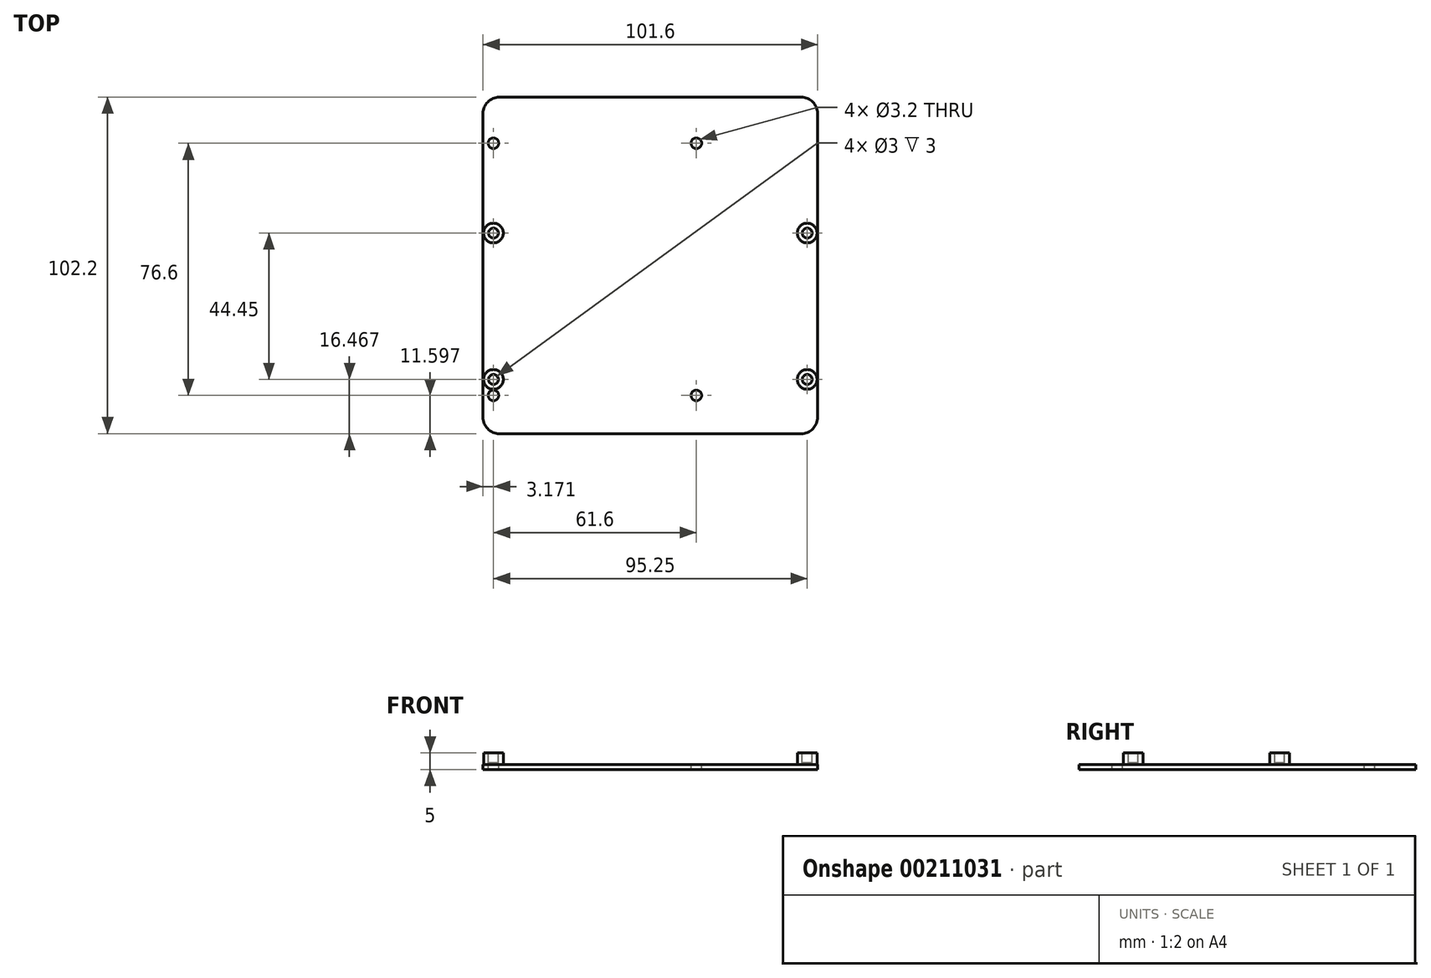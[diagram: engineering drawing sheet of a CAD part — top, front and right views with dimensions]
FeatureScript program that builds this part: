
annotation { "Feature Type Name" : "Feature", "Feature Type Description" : "" }
export const myFeature = defineFeature(function(context is Context, id is Id, definition is map)
    precondition{}
    {
        {
            var Q0;
            Q0=qCreatedBy(makeId("Top.planeOp"),FACE);
            var sketch = newSketch(context, id + "F0", { "sketchPlane" : qUnion([Q0])});
            skLineSegment(sketch, "E0.bottom", {"start": v(-70.53, 110.53) * mm, "end": v(31.07, 110.53) * mm});
            skLineSegment(sketch, "E0.top", {"start": v(-70.53, -36.47) * mm, "end": v(31.07, -36.47) * mm});
            skLineSegment(sketch, "E0.left", {"start": v(-70.53, 110.53) * mm, "end": v(-70.53, -36.47) * mm});
            skLineSegment(sketch, "E0.right", {"start": v(31.07, 110.53) * mm, "end": v(31.07, -36.47) * mm});
            skCircle(sketch, "E1", {"center": v(-67.36, 69.25) * mm, "radius": 3 * mm});
            skCircle(sketch, "E2", {"center": v(27.9, 69.25) * mm, "radius": 3 * mm});
            skCircle(sketch, "E3", {"center": v(-67.36, 24.8) * mm, "radius": 3 * mm});
            skCircle(sketch, "E4", {"center": v(27.9, 24.8) * mm, "radius": 3 * mm});
            skSolve(sketch);
        }
        {
            var Q0;
            Q0=makeQuery(id+"F0.imprint","IMPRINT",FACE,{"disambiguationData":[TD([[makeQuery(id+"F0.imprint","IMPRINT",EDGE,{"derivedFrom":sQuery(id+"F0.wireOp",EDGE,"E1")}),-1.0]])]});
            var Q1;
            {var subQ8=sQuery(id+"F0.wireOp",EDGE,"E0.bottom");Q1=makeQuery(id+"F0.imprint","IMPRINT",FACE,{"disambiguationData":[TD([[makeQuery(id+"F0.imprint","IMPRINT",EDGE,{"derivedFrom":subQ8}),-1.0]])]});}
            var Q2;
            Q2=makeQuery(id+"F0.imprint","IMPRINT",FACE,{"disambiguationData":[TD([[makeQuery(id+"F0.imprint","IMPRINT",EDGE,{"derivedFrom":sQuery(id+"F0.wireOp",EDGE,"E3")}),-1.0]])]});
            var Q3;
            Q3=makeQuery(id+"F0.imprint","IMPRINT",FACE,{"disambiguationData":[TD([[makeQuery(id+"F0.imprint","IMPRINT",EDGE,{"derivedFrom":sQuery(id+"F0.wireOp",EDGE,"E2")}),-1.0]])]});
            var Q4;
            Q4=makeQuery(id+"F0.imprint","IMPRINT",FACE,{"disambiguationData":[TD([[makeQuery(id+"F0.imprint","IMPRINT",EDGE,{"derivedFrom":sQuery(id+"F0.wireOp",EDGE,"E4")}),-1.0]])]});
            var Q5;
            {var subQ0=sQuery(id+"F0.wireOp",EDGE,"LZDnmpIZ-xvqJ-npT3-o2hn-prvxRaRxMuR7");var subQ1=sQuery(id+"F0.wireOp",EDGE,"E0.right");var subQ2=makeQuery(id+"F0.imprint","INTERSECT",VERTEX,{"disambiguationData":[OD(0.0)],"derivedFrom":[subQ1,subQ0]});Q5=makeQuery(id+"F0.imprint","IMPRINT",FACE,{"disambiguationData":[TD([[makeQuery(id+"F0.imprint","IMPRINT",EDGE,{"disambiguationData":[TD([[subQ2,-1.0]])],"derivedFrom":subQ1}),1.0]])]});}
            var Q6;
            {var subQ0=sQuery(id+"F0.wireOp",EDGE,"yrvKWCMc-wCms-miBF-EHxo-dlBtZxVLjjzE");var subQ1=sQuery(id+"F0.wireOp",EDGE,"E0.right");var subQ2=makeQuery(id+"F0.imprint","INTERSECT",VERTEX,{"disambiguationData":[OD(0.0)],"derivedFrom":[subQ1,subQ0]});Q6=makeQuery(id+"F0.imprint","IMPRINT",FACE,{"disambiguationData":[TD([[makeQuery(id+"F0.imprint","IMPRINT",EDGE,{"disambiguationData":[TD([[subQ2,-1.0]])],"derivedFrom":subQ1}),1.0]])]});}
            extrude(context, id + "F1", {"entities" : qUnion([Q0, Q1, Q2, Q3, Q4, Q5, Q6]), "depth" : 1.5 * mm});
        }
        {
            var Q0;
            Q0=makeQuery(id+"F1.opExtrude","CAP_FACE",FACE,{"disambiguationData":[OSD([sQuery(id+"F0.wireOp",EDGE,"E0.bottom"),sQuery(id+"F0.wireOp",EDGE,"E0.top"),sQuery(id+"F0.wireOp",EDGE,"E0.left"),sQuery(id+"F0.wireOp",EDGE,"E0.right"),sQuery(id+"F0.wireOp",EDGE,"E1"),sQuery(id+"F0.wireOp",EDGE,"E2"),sQuery(id+"F0.wireOp",EDGE,"E3"),sQuery(id+"F0.wireOp",EDGE,"E4"),sQuery(id+"F0.wireOp",EDGE,"YPoFhnEZ-2VS0-5aPg-Brrl-id8hAxNxdBGg"),sQuery(id+"F0.wireOp",EDGE,"uQWfn0jv-DCcC-0w1e-9Akf-fMqCXPyrSpFM"),sQuery(id+"F0.wireOp",EDGE,"LZDnmpIZ-xvqJ-npT3-o2hn-prvxRaRxMuR7"),sQuery(id+"F0.wireOp",EDGE,"yrvKWCMc-wCms-miBF-EHxo-dlBtZxVLjjzE")])],"isStart":false});
            var sketch = newSketch(context, id + "F2", { "sketchPlane" : qUnion([Q0])});
            skPoint(sketch, "E5.0", {"position": v(-67.36, 69.25) * mm});
            skCircle(sketch, "E6", {"center": v(-67.36, 96.53) * mm, "radius": 1.6 * mm});
            skCircle(sketch, "E7", {"center": v(-67.36, 19.93) * mm, "radius": 1.6 * mm});
            skCircle(sketch, "E8", {"center": v(-5.76, 96.53) * mm, "radius": 1.6 * mm});
            skCircle(sketch, "E9", {"center": v(-5.76, 19.93) * mm, "radius": 1.6 * mm});
            skSolve(sketch);
        }
        {
            var Q0;
            Q0=makeQuery(id+"F2.imprint","IMPRINT",FACE,{"disambiguationData":[TD([[makeQuery(id+"F2.imprint","IMPRINT",EDGE,{"derivedFrom":sQuery(id+"F2.wireOp",EDGE,"E6")}),1.0]])]});
            var Q1;
            Q1=makeQuery(id+"F2.imprint","IMPRINT",FACE,{"disambiguationData":[TD([[makeQuery(id+"F2.imprint","IMPRINT",EDGE,{"derivedFrom":sQuery(id+"F2.wireOp",EDGE,"E8")}),1.0]])]});
            var Q2;
            Q2=makeQuery(id+"F2.imprint","IMPRINT",FACE,{"disambiguationData":[TD([[makeQuery(id+"F2.imprint","IMPRINT",EDGE,{"derivedFrom":sQuery(id+"F2.wireOp",EDGE,"E7")}),1.0]])]});
            var Q3;
            Q3=makeQuery(id+"F2.imprint","IMPRINT",FACE,{"disambiguationData":[TD([[makeQuery(id+"F2.imprint","IMPRINT",EDGE,{"derivedFrom":sQuery(id+"F2.wireOp",EDGE,"E9")}),1.0]])]});
            extrude(context, id + "F3", {"entities" : qUnion([Q0, Q1, Q2, Q3]), "operationType" : NewBodyOperationType.REMOVE, "oppositeDirection" : true, "depth" : 25 * mm});
        }
        {
            var Q0;
            Q0=makeQuery(id+"F0.imprint","IMPRINT",FACE,{"disambiguationData":[TD([[makeQuery(id+"F0.imprint","IMPRINT",EDGE,{"derivedFrom":sQuery(id+"F0.wireOp",EDGE,"E1")}),1.0]])]});
            var Q1;
            Q1=makeQuery(id+"F0.imprint","IMPRINT",FACE,{"disambiguationData":[TD([[makeQuery(id+"F0.imprint","IMPRINT",EDGE,{"derivedFrom":sQuery(id+"F0.wireOp",EDGE,"E3")}),1.0]])]});
            var Q2;
            Q2=makeQuery(id+"F0.imprint","IMPRINT",FACE,{"disambiguationData":[TD([[makeQuery(id+"F0.imprint","IMPRINT",EDGE,{"derivedFrom":sQuery(id+"F0.wireOp",EDGE,"E2")}),1.0]])]});
            var Q3;
            Q3=makeQuery(id+"F0.imprint","IMPRINT",FACE,{"disambiguationData":[TD([[makeQuery(id+"F0.imprint","IMPRINT",EDGE,{"derivedFrom":sQuery(id+"F0.wireOp",EDGE,"E4")}),1.0]])]});
            extrude(context, id + "F4", {"entities" : qUnion([Q0, Q1, Q2, Q3]), "operationType" : NewBodyOperationType.ADD, "depth" : 5 * mm});
        }
        {
            var Q0;
            Q0=makeQuery(id+"F4.opExtrude","CAP_FACE",FACE,{"disambiguationData":[OSD([sQuery(id+"F0.wireOp",EDGE,"E1")])],"isStart":false});
            var sketch = newSketch(context, id + "F5", { "sketchPlane" : qUnion([Q0])});
            skPoint(sketch, "E10.0", {"position": v(-67.36, 69.25) * mm});
            skPoint(sketch, "E10.1", {"position": v(-67.36, 24.8) * mm});
            skCircle(sketch, "E11", {"center": v(-67.36, 69.25) * mm, "radius": 1.5 * mm});
            skCircle(sketch, "E12", {"center": v(-67.36, 24.8) * mm, "radius": 1.5 * mm});
            skPoint(sketch, "E13.0", {"position": v(27.9, 69.25) * mm});
            skPoint(sketch, "E13.1", {"position": v(27.9, 24.8) * mm});
            skCircle(sketch, "E14", {"center": v(27.9, 69.25) * mm, "radius": 1.5 * mm});
            skCircle(sketch, "E15", {"center": v(27.9, 24.8) * mm, "radius": 1.5 * mm});
            skSolve(sketch);
        }
        {
            var Q0;
            Q0=makeQuery(id+"F5.imprint","IMPRINT",FACE,{"disambiguationData":[TD([[makeQuery(id+"F5.imprint","IMPRINT",EDGE,{"derivedFrom":sQuery(id+"F5.wireOp",EDGE,"E11")}),1.0]])]});
            var Q1;
            Q1=makeQuery(id+"F5.imprint","IMPRINT",FACE,{"disambiguationData":[TD([[makeQuery(id+"F5.imprint","IMPRINT",EDGE,{"derivedFrom":sQuery(id+"F5.wireOp",EDGE,"E12")}),1.0]])]});
            var Q2;
            Q2=makeQuery(id+"F5.imprint","IMPRINT",FACE,{"disambiguationData":[TD([[makeQuery(id+"F5.imprint","IMPRINT",EDGE,{"derivedFrom":sQuery(id+"F5.wireOp",EDGE,"E14")}),1.0]])]});
            var Q3;
            Q3=makeQuery(id+"F5.imprint","IMPRINT",FACE,{"disambiguationData":[TD([[makeQuery(id+"F5.imprint","IMPRINT",EDGE,{"derivedFrom":sQuery(id+"F5.wireOp",EDGE,"E15")}),1.0]])]});
            extrude(context, id + "F6", {"entities" : qUnion([Q0, Q1, Q2, Q3]), "operationType" : NewBodyOperationType.REMOVE, "oppositeDirection" : true, "depth" : 3 * mm});
        }
        {
            var Q0;
            Q0=makeQuery(id+"F1.opExtrude","CAP_FACE",FACE,{"disambiguationData":[OSD([sQuery(id+"F0.wireOp",EDGE,"E0.bottom"),sQuery(id+"F0.wireOp",EDGE,"E0.top"),sQuery(id+"F0.wireOp",EDGE,"E0.left"),sQuery(id+"F0.wireOp",EDGE,"E0.right"),sQuery(id+"F0.wireOp",EDGE,"E1"),sQuery(id+"F0.wireOp",EDGE,"E2"),sQuery(id+"F0.wireOp",EDGE,"E3"),sQuery(id+"F0.wireOp",EDGE,"E4")])],"isStart":false});
            var sketch = newSketch(context, id + "F7", { "sketchPlane" : qUnion([Q0])});
            skLineSegment(sketch, "E16.bottom", {"start": v(-108.6, 8.33) * mm, "end": v(74.7, 8.33) * mm});
            skLineSegment(sketch, "E16.top", {"start": v(-108.6, -69.36) * mm, "end": v(74.7, -69.36) * mm});
            skLineSegment(sketch, "E16.left", {"start": v(-108.6, 8.33) * mm, "end": v(-108.6, -69.36) * mm});
            skLineSegment(sketch, "E16.right", {"start": v(74.7, 8.33) * mm, "end": v(74.7, -69.36) * mm});
            skLineSegment(sketch, "E17.bottom", {"start": v(-108.17, 119.73) * mm, "end": v(58.54, 119.73) * mm});
            skLineSegment(sketch, "E17.top", {"start": v(-108.17, 100.53) * mm, "end": v(58.54, 100.53) * mm});
            skLineSegment(sketch, "E17.left", {"start": v(-108.17, 119.73) * mm, "end": v(-108.17, 100.53) * mm});
            skLineSegment(sketch, "E17.right", {"start": v(58.54, 119.73) * mm, "end": v(58.54, 100.53) * mm});
            skSolve(sketch);
        }
        {
            var Q0;
            {var subQ5=makeQuery(id+"F1.opExtrude","CAP_EDGE",EDGE,{"disambiguationData":[OSD([sQuery(id+"F0.wireOp",EDGE,"E0.top")])],"isStart":false});Q0=makeQuery(id+"F7.imprint","IMPRINT",FACE,{"disambiguationData":[TD([[makeQuery(id+"F7.imprint","IMPRINT",EDGE,{"derivedFrom":subQ5}),1.0]])]});}
            var Q1;
            Q1=makeQuery(id+"F7.imprint","IMPRINT",FACE,{"disambiguationData":[TD([[makeQuery(id+"F7.imprint","IMPRINT",EDGE,{"derivedFrom":sQuery(id+"F7.wireOp",EDGE,"E16.top")}),1.0]])]});
            var Q2;
            Q2=makeQuery(id+"F7.imprint","IMPRINT",FACE,{"disambiguationData":[TD([[makeQuery(id+"F7.imprint","IMPRINT",EDGE,{"derivedFrom":sQuery(id+"F7.wireOp",EDGE,"E17.bottom")}),-1.0]])]});
            extrude(context, id + "F8", {"entities" : qUnion([Q0, Q1, Q2]), "operationType" : NewBodyOperationType.REMOVE, "oppositeDirection" : true, "depth" : 25 * mm});
        }
        {
            var Q0;
            Q0=makeQuery(id+"F8.boolean.opBoolean","INTERSECT",EDGE,{"derivedFrom":[makeQuery(id+"F1.opExtrude","SWEPT_FACE",FACE,{"disambiguationData":[OSD([sQuery(id+"F0.wireOp",EDGE,"E0.left")])]}),makeQuery(id+"F8.opExtrude","SWEPT_FACE",FACE,{"disambiguationData":[OSD([sQuery(id+"F7.wireOp",EDGE,"E16.bottom")])]})]});
            var Q1;
            Q1=makeQuery(id+"F1.opExtrude","SWEPT_EDGE",EDGE,{"disambiguationData":[OSD([sQuery(id+"F0.wireOp",EDGE,"E0.bottom"),sQuery(id+"F0.wireOp",EDGE,"E0.left")])]});
            var Q2;
            Q2=makeQuery(id+"F8.boolean.opBoolean","INTERSECT",EDGE,{"derivedFrom":[makeQuery(id+"F1.opExtrude","SWEPT_FACE",FACE,{"disambiguationData":[OSD([sQuery(id+"F0.wireOp",EDGE,"E0.right")])]}),makeQuery(id+"F8.opExtrude","SWEPT_FACE",FACE,{"disambiguationData":[OSD([sQuery(id+"F7.wireOp",EDGE,"E16.bottom")])]})]});
            var Q3;
            Q3=makeQuery(id+"F1.opExtrude","SWEPT_EDGE",EDGE,{"disambiguationData":[OSD([sQuery(id+"F0.wireOp",EDGE,"E0.bottom"),sQuery(id+"F0.wireOp",EDGE,"E0.right")])]});
            fillet(context, id + "F9", {"entities" : qUnion([Q0, Q1, Q2, Q3]), "radius" : 5 * mm, "tangentPropagation" : true, "allowEdgeOverflow" : false});
        }
    });
